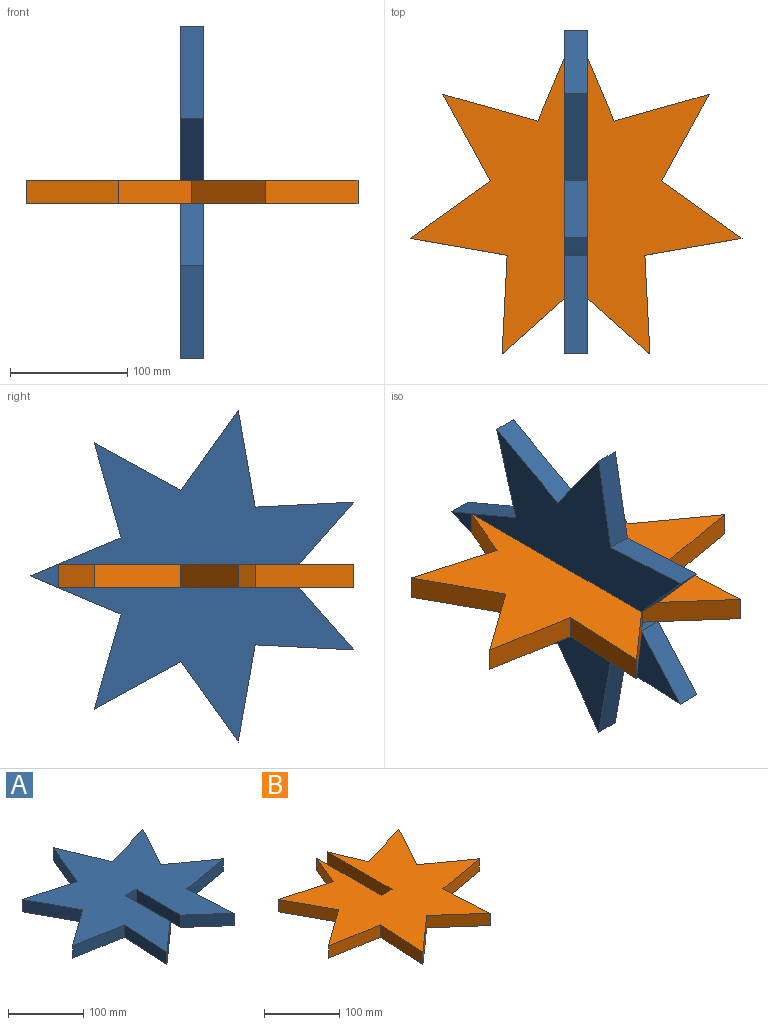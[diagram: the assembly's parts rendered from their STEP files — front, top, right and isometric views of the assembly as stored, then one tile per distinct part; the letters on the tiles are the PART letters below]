
ASSEMBLY  parts=2 mates=1
PART A: 19 faces, bbox 282.7x275.6x20 mm
  f0: plane 282.73x275.64mm, normal (0,0,1), area 31441mm2, adj f2,f3,f4,f5,f6,f7,f8,f9
  f1: plane 282.73x275.64mm, normal (0,0,-1), area 31441mm2, adj f2,f3,f4,f5,f6,f7,f8,f9
  f2: plane 68.25x48.95mm, normal (-0.58,0.81,0), area 1679.8mm2, adj f0,f1,f3,f15
  f3: plane 82.73x20mm, normal (-0.17,-0.98,0), area 1679.8mm2, adj f0,f1,f2,f4
  f4: plane 83.88x20mm, normal (-1,0.05,0), area 1679.8mm2, adj f0,f1,f3,f5
  f5: plane 52.91x46.8mm, normal (0.66,-0.75,0), area 1412.8mm2, adj f0,f1,f4,f16
  f6: plane 52.91x46.8mm, normal (-0.66,-0.75,0), area 1412.8mm2, adj f0,f1,f7,f17
  f7: plane 83.88x20mm, normal (1,0.05,0), area 1679.8mm2, adj f0,f1,f6,f8
  f8: plane 82.73x20mm, normal (0.17,-0.98,0), area 1679.8mm2, adj f0,f1,f7,f9
  f9: plane 68.25x48.95mm, normal (0.58,0.81,0), area 1679.8mm2, adj f0,f1,f8,f10
  f10: plane 73.72x40.25mm, normal (0.88,-0.48,0), area 1679.8mm2, adj f0,f1,f9,f11
  f11: plane 80.82x22.83mm, normal (-0.27,0.96,0), area 1679.8mm2, adj f0,f1,f10,f12
  f12: plane 77.43x32.54mm, normal (0.92,0.39,0), area 1679.8mm2, adj f0,f1,f11,f13
  f13: plane 77.43x32.54mm, normal (-0.92,0.39,0), area 1679.8mm2, adj f0,f1,f12,f14
  f14: plane 80.82x22.83mm, normal (0.27,0.96,0), area 1679.8mm2, adj f0,f1,f13,f15
  f15: plane 73.72x40.25mm, normal (-0.88,-0.48,0), area 1679.8mm2, adj f0,f1,f2,f14
  f16: plane 83.84x20mm, normal (1,0,0), area 1676.9mm2, adj f0,f1,f5,f18
  f17: plane 83.84x20mm, normal (-1,0,0), area 1676.9mm2, adj f0,f1,f6,f18
  f18: plane 20x20mm, normal (0,-1,0), area 400mm2, adj f0,f1,f16,f17
PART B: 19 faces, bbox 282.7x251.8x20 mm
  f0: plane 53.63x22.54mm, normal (0.92,0.39,0), area 1163.6mm2, adj f10,f14,f15,f18
  f1: plane 68.25x48.95mm, normal (-0.58,0.81,0), area 1679.8mm2, adj f2,f13,f14,f15
  f2: plane 82.73x20mm, normal (-0.17,-0.98,0), area 1679.8mm2, adj f1,f3,f14,f15
  f3: plane 83.88x20mm, normal (-1,0.05,0), area 1679.8mm2, adj f2,f4,f14,f15
  f4: plane 62.91x55.64mm, normal (0.66,-0.75,0), area 1679.8mm2, adj f3,f5,f14,f15
  f5: plane 62.91x55.64mm, normal (-0.66,-0.75,0), area 1679.8mm2, adj f4,f6,f14,f15
  f6: plane 83.88x20mm, normal (1,0.05,0), area 1679.8mm2, adj f5,f7,f14,f15
  f7: plane 82.73x20mm, normal (0.17,-0.98,0), area 1679.8mm2, adj f6,f8,f14,f15
  f8: plane 68.25x48.95mm, normal (0.58,0.81,0), area 1679.8mm2, adj f7,f9,f14,f15
  f9: plane 73.72x40.25mm, normal (0.88,-0.48,0), area 1679.8mm2, adj f8,f10,f14,f15
  f10: plane 80.82x22.83mm, normal (-0.27,0.96,0), area 1679.8mm2, adj f0,f9,f14,f15
  f11: plane 53.63x22.54mm, normal (-0.92,0.39,0), area 1163.6mm2, adj f12,f14,f15,f16
  f12: plane 80.82x22.83mm, normal (0.27,0.96,0), area 1679.8mm2, adj f11,f13,f14,f15
  f13: plane 73.72x40.25mm, normal (-0.88,-0.48,0), area 1679.8mm2, adj f1,f12,f14,f15
  f14: plane 282.73x251.85mm, normal (0,0,1), area 30367.3mm2, adj f0,f1,f2,f3,f4,f5,f6,f7
  f15: plane 282.73x251.85mm, normal (0,0,-1), area 30367.3mm2, adj f0,f1,f2,f3,f4,f5,f6,f7
  f16: plane 121.21x20mm, normal (1,0,0), area 2424.1mm2, adj f11,f14,f15,f17
  f17: plane 20x20mm, normal (0,1,0), area 400mm2, adj f14,f15,f16,f18
  f18: plane 121.21x20mm, normal (-1,0,0), area 2424.1mm2, adj f0,f14,f15,f17
PLACE A rot(axis=(0,1,0),90deg) t=(106.39,130.16,-14.66)mm
PLACE B t=(116.39,130.06,-24.66)mm fixed
MATE slider A.f18 <-> B.f17  axis (0,-1,0) through (116.39,130.16,-14.66)mm
